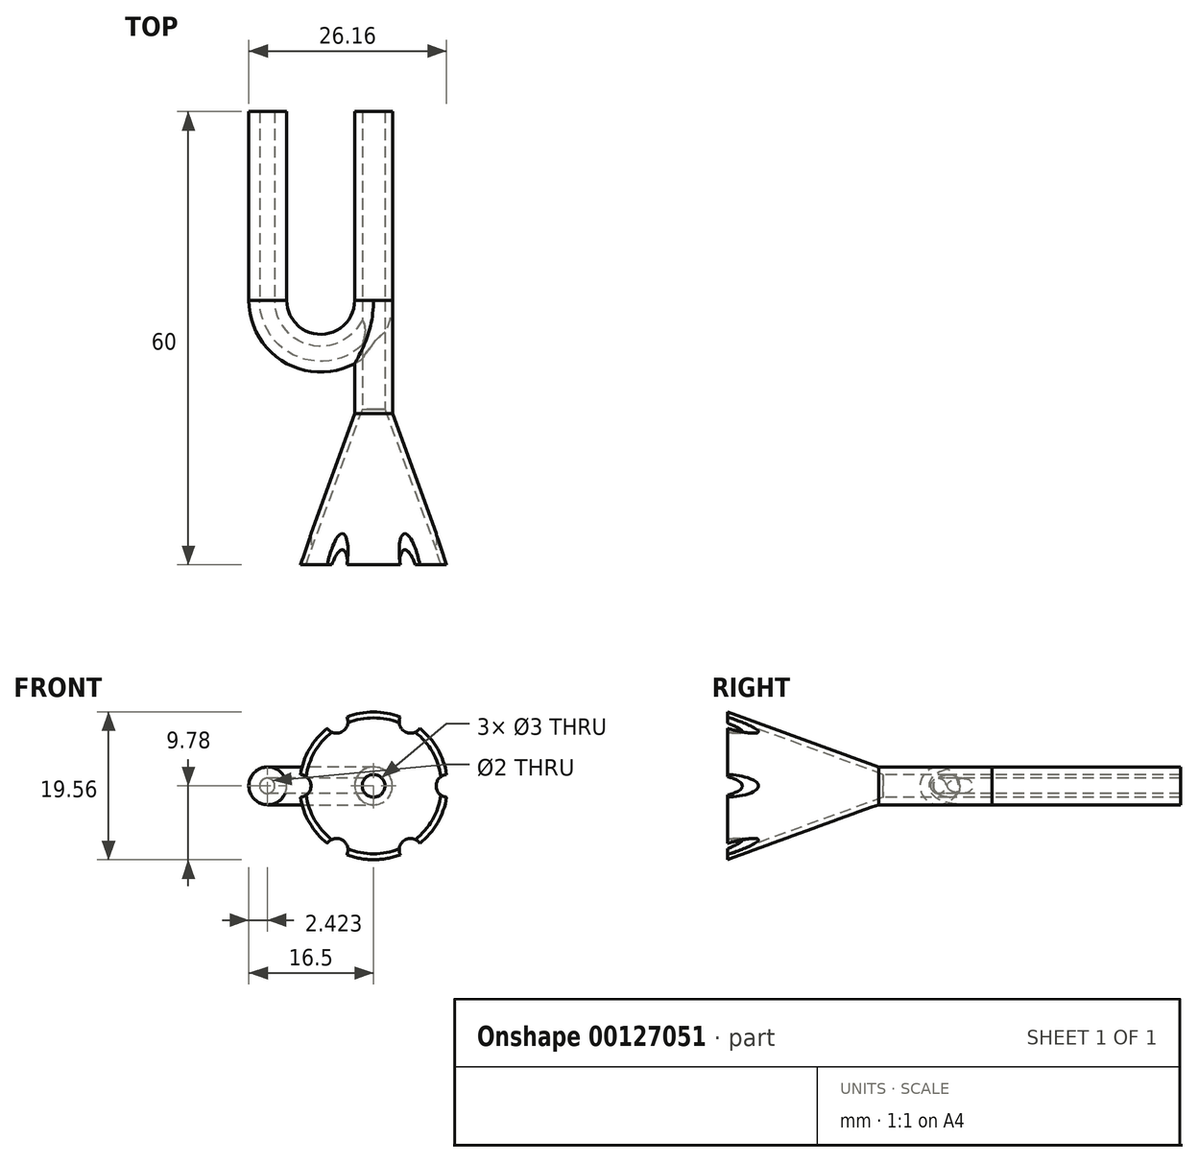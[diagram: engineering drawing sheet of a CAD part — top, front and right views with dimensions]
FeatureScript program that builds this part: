
annotation { "Feature Type Name" : "Feature", "Feature Type Description" : "" }
export const myFeature = defineFeature(function(context is Context, id is Id, definition is map)
    precondition{}
    {
        {
            var Q0;
            Q0=qCreatedBy(makeId("Top.planeOp"),FACE);
            var sketch = newSketch(context, id + "F0", { "sketchPlane" : qUnion([Q0])});
            skLineSegment(sketch, "E0.bottom", {"start": v(-11.15, 0) * mm, "end": v(11.15, 0) * mm});
            skLineSegment(sketch, "E0.top", {"start": v(-11.15, -35) * mm, "end": v(11.15, -35) * mm});
            skLineSegment(sketch, "E0.left", {"start": v(-11.15, 0) * mm, "end": v(-11.15, -35) * mm});
            skLineSegment(sketch, "E0.right", {"start": v(11.15, 0) * mm, "end": v(11.15, -35) * mm});
            skSolve(sketch);
        }
        {
            var Q0;
            Q0=qCreatedBy(makeId("Front.planeOp"),FACE);
            var sketch = newSketch(context, id + "F1", { "sketchPlane" : qUnion([Q0])});
            skCircle(sketch, "E1", {"center": v(7, 0) * mm, "radius": 2.5 * mm});
            skCircle(sketch, "E2", {"center": v(-7, 0) * mm, "radius": 2.5 * mm});
            skSolve(sketch);
        }
        {
            var Q0;
            Q0=makeQuery(id+"F1.imprint","IMPRINT",FACE,{"disambiguationData":[TD([[makeQuery(id+"F1.imprint","IMPRINT",EDGE,{"derivedFrom":sQuery(id+"F1.wireOp",EDGE,"E1")}),1.0]])]});
            extrude(context, id + "F2", {"entities" : qUnion([Q0]), "oppositeDirection" : true, "depth" : 25 * mm});
        }
        {
            var Q0;
            Q0=makeQuery(id+"F2.opExtrude","CAP_FACE",FACE,{"disambiguationData":[OSD([sQuery(id+"F1.wireOp",EDGE,"E1")])],"isStart":true});
            var sketch = newSketch(context, id + "F3", { "sketchPlane" : qUnion([Q0])});
            skCircle(sketch, "E3", {"center": v(7, 0) * mm, "radius": 1.5 * mm});
            skSolve(sketch);
        }
        {
            var Q0;
            Q0=makeQuery(id+"F1.imprint","IMPRINT",FACE,{"disambiguationData":[TD([[makeQuery(id+"F1.imprint","IMPRINT",EDGE,{"derivedFrom":sQuery(id+"F1.wireOp",EDGE,"E2")}),1.0]])]});
            var Q1;
            Q1=sQuery(id+"F1.wireOp",EDGE,"E2");
            extrude(context, id + "F4", {"entities" : qUnion([Q0]), "operationType" : NewBodyOperationType.ADD, "surfaceEntities" : qUnion([Q1]), "oppositeDirection" : true, "depth" : 25 * mm});
        }
        {
            var Q0;
            Q0=makeQuery(id+"F1.imprint","IMPRINT",FACE,{"disambiguationData":[TD([[makeQuery(id+"F1.imprint","IMPRINT",EDGE,{"derivedFrom":sQuery(id+"F1.wireOp",EDGE,"E2")}),1.0]])]});
            var sketch = newSketch(context, id + "F5", { "sketchPlane" : qUnion([Q0])});
            skCircle(sketch, "E4", {"center": v(-7.08, 0) * mm, "radius": 1 * mm});
            skSolve(sketch);
        }
        {
            var Q0;
            Q0 = qSketchRegion(id + "F5", true);
            extrude(context, id + "F6", {"entities" : qUnion([Q0]), "operationType" : NewBodyOperationType.REMOVE, "endBound" : BoundingType.THROUGH_ALL, "oppositeDirection" : true, "depth" : 25 * mm});
        }
        {
            var Q0;
            Q0=qCreatedBy(makeId("Top.planeOp"),FACE);
            var sketch = newSketch(context, id + "F7", { "sketchPlane" : qUnion([Q0])});
            skArc(sketch, "E5", {"start": v(-7, 0) * mm, "mid": v(0, -7) * mm, "end": v(7, 0) * mm});
            skSolve(sketch);
        }
        {
            var Q0;
            Q0=makeQuery(id+"F5.imprint","IMPRINT",FACE,{"disambiguationData":[TD([[makeQuery(id+"F5.imprint","IMPRINT",EDGE,{"derivedFrom":sQuery(id+"F5.wireOp",EDGE,"E4")}),-1.0]])]});
            var Q1;
            Q1=sQuery(id+"F7.wireOp",EDGE,"E5");
            sweep(context, id + "F8", {"profiles" : qUnion([Q0]), "path" : qUnion([Q1])});
        }
        {
            var Q0;
            Q0 = qSketchRegion(id + "F3", true);
            extrude(context, id + "F9", {"entities" : qUnion([Q0]), "operationType" : NewBodyOperationType.REMOVE, "oppositeDirection" : true, "depth" : 50 * mm, "symmetric" : true});
        }
        {
            var Q0;
            Q0=qCreatedBy(makeId("Front.planeOp"),FACE);
            cPlane(context, id + "F10", {"entities" : qUnion([Q0]), "cplaneType" : CPlaneType.OFFSET, "offset" : 15 * mm, "width" : 150 * mm, "height" : 150 * mm});
        }
        {
            var Q0;
            Q0=qCreatedBy(id+"F10.planeOp",FACE);
            var sketch = newSketch(context, id + "F11", { "sketchPlane" : qUnion([Q0])});
            skCircle(sketch, "E6", {"center": v(7, 0) * mm, "radius": 2.5 * mm});
            skSolve(sketch);
        }
        {
            var Q0;
            Q0=makeQuery(id+"F11.imprint","IMPRINT",FACE,{"disambiguationData":[TD([[makeQuery(id+"F11.imprint","IMPRINT",EDGE,{"derivedFrom":sQuery(id+"F11.wireOp",EDGE,"E6")}),1.0]])]});
            var Q1;
            Q1=makeQuery(id+"F8.opSweep","SWEPT_FACE",FACE,{"disambiguationData":[OSD([sQuery(id+"F1.wireOp",EDGE,"E2"),sQuery(id+"F7.wireOp",EDGE,"E5")])]});
            extrude(context, id + "F12", {"entities" : qUnion([Q0]), "endBound" : BoundingType.UP_TO_SURFACE, "oppositeDirection" : true, "endBoundEntityFace" : qUnion([Q1]), "depth" : 25 * mm});
        }
        {
            var Q0;
            Q0=makeQuery(id+"F12.opExtrude","CAP_FACE",FACE,{"disambiguationData":[OSD([sQuery(id+"F11.wireOp",EDGE,"E6")])],"isStart":true});
            var sketch = newSketch(context, id + "F13", { "sketchPlane" : qUnion([Q0])});
            skCircle(sketch, "E7", {"center": v(7, 0) * mm, "radius": 1.5 * mm});
            skSolve(sketch);
        }
        {
            var Q0;
            Q0 = qSketchRegion(id + "F13", true);
            var Q1;
            Q1=makeQuery(id+"F8.opSweep","SWEPT_FACE",FACE,{"disambiguationData":[OSD([sQuery(id+"F1.wireOp",EDGE,"E2"),sQuery(id+"F7.wireOp",EDGE,"E5")])]});
            extrude(context, id + "F14", {"entities" : qUnion([Q0]), "operationType" : NewBodyOperationType.REMOVE, "endBound" : BoundingType.UP_TO_SURFACE, "oppositeDirection" : true, "endBoundEntityFace" : qUnion([Q1]), "depth" : 25 * mm});
        }
        {
            var Q0;
            Q0=makeQuery(id+"F13.imprint","IMPRINT",FACE,{"disambiguationData":[TD([[makeQuery(id+"F13.imprint","IMPRINT",EDGE,{"derivedFrom":sQuery(id+"F13.wireOp",EDGE,"E7")}),-1.0]])]});
            extrude(context, id + "F15", {"entities" : qUnion([Q0]), "operationType" : NewBodyOperationType.ADD, "depth" : 20 * mm, "hasDraft" : true, "draftAngle" : 20 * degree});
        }
        {
            var Q0;
            Q0=makeQuery(id+"F15.opExtrude","CAP_FACE",FACE,{"disambiguationData":[OSD([sQuery(id+"F11.wireOp",EDGE,"E6"),sQuery(id+"F13.wireOp",EDGE,"E7")])],"isStart":false});
            var sketch = newSketch(context, id + "F16", { "sketchPlane" : qUnion([Q0])});
            skCircle(sketch, "E8", {"center": v(7, 0) * mm, "radius": 9 * mm});
            skCircle(sketch, "E9", {"center": v(-2.78, 0) * mm, "radius": 1.5 * mm});
            skCircle(sketch, "E10.1.0", {"center": v(2.11, 8.47) * mm, "radius": 1.5 * mm});
            skCircle(sketch, "E10.2.0", {"center": v(11.89, 8.47) * mm, "radius": 1.5 * mm});
            skCircle(sketch, "E10.3.0", {"center": v(16.78, 0) * mm, "radius": 1.5 * mm});
            skCircle(sketch, "E10.4.0", {"center": v(11.89, -8.47) * mm, "radius": 1.5 * mm});
            skCircle(sketch, "E10.5.0", {"center": v(2.11, -8.47) * mm, "radius": 1.5 * mm});
            skLineSegment(sketch, "E10.anchor1", {"start": v(7, 0) * mm, "end": v(-2.78, 0) * mm, "construction": true});
            skLineSegment(sketch, "E10.anchor2", {"start": v(7, 0) * mm, "end": v(2.11, -8.47) * mm, "construction": true});
            skSolve(sketch);
        }
        {
            var Q0;
            {var subQ0=sQuery(id+"F16.wireOp",EDGE,"E10.3.0");var subQ1=sQuery(id+"F16.wireOp",EDGE,"E8");var subQ2=makeQuery(id+"F16.imprint","INTERSECT",VERTEX,{"disambiguationData":[OD(0.0)],"derivedFrom":[subQ1,subQ0]});Q0=makeQuery(id+"F16.imprint","IMPRINT",FACE,{"disambiguationData":[TD([[makeQuery(id+"F16.imprint","IMPRINT",EDGE,{"disambiguationData":[TD([[subQ2,1.0]])],"derivedFrom":subQ1}),1.0]])]});}
            var Q1;
            {var subQ0=sQuery(id+"F16.wireOp",EDGE,"E10.4.0");var subQ1=sQuery(id+"F16.wireOp",EDGE,"E8");var subQ2=makeQuery(id+"F16.imprint","INTERSECT",VERTEX,{"disambiguationData":[OD(0.0)],"derivedFrom":[subQ1,subQ0]});Q1=makeQuery(id+"F16.imprint","IMPRINT",FACE,{"disambiguationData":[TD([[makeQuery(id+"F16.imprint","IMPRINT",EDGE,{"disambiguationData":[TD([[subQ2,-1.0]])],"derivedFrom":subQ1}),1.0]])]});}
            var Q2;
            {var subQ0=sQuery(id+"F16.wireOp",EDGE,"E10.5.0");var subQ1=sQuery(id+"F16.wireOp",EDGE,"E8");var subQ2=makeQuery(id+"F16.imprint","INTERSECT",VERTEX,{"disambiguationData":[OD(0.0)],"derivedFrom":[subQ1,subQ0]});Q2=makeQuery(id+"F16.imprint","IMPRINT",FACE,{"disambiguationData":[TD([[makeQuery(id+"F16.imprint","IMPRINT",EDGE,{"disambiguationData":[TD([[subQ2,-1.0]])],"derivedFrom":subQ1}),1.0]])]});}
            var Q3;
            {var subQ0=sQuery(id+"F16.wireOp",EDGE,"E9");var subQ1=sQuery(id+"F16.wireOp",EDGE,"E8");var subQ2=makeQuery(id+"F16.imprint","INTERSECT",VERTEX,{"disambiguationData":[OD(0.0)],"derivedFrom":[subQ1,subQ0]});Q3=makeQuery(id+"F16.imprint","IMPRINT",FACE,{"disambiguationData":[TD([[makeQuery(id+"F16.imprint","IMPRINT",EDGE,{"disambiguationData":[TD([[subQ2,-1.0]])],"derivedFrom":subQ1}),1.0]])]});}
            var Q4;
            {var subQ0=sQuery(id+"F16.wireOp",EDGE,"E10.1.0");var subQ1=sQuery(id+"F16.wireOp",EDGE,"E8");var subQ2=makeQuery(id+"F16.imprint","INTERSECT",VERTEX,{"disambiguationData":[OD(0.0)],"derivedFrom":[subQ1,subQ0]});Q4=makeQuery(id+"F16.imprint","IMPRINT",FACE,{"disambiguationData":[TD([[makeQuery(id+"F16.imprint","IMPRINT",EDGE,{"disambiguationData":[TD([[subQ2,-1.0]])],"derivedFrom":subQ1}),1.0]])]});}
            var Q5;
            {var subQ0=sQuery(id+"F16.wireOp",EDGE,"E10.2.0");var subQ1=sQuery(id+"F16.wireOp",EDGE,"E8");var subQ2=makeQuery(id+"F16.imprint","INTERSECT",VERTEX,{"disambiguationData":[OD(0.0)],"derivedFrom":[subQ1,subQ0]});Q5=makeQuery(id+"F16.imprint","IMPRINT",FACE,{"disambiguationData":[TD([[makeQuery(id+"F16.imprint","IMPRINT",EDGE,{"disambiguationData":[TD([[subQ2,-1.0]])],"derivedFrom":subQ1}),1.0]])]});}
            var Q6;
            {var subQ0=sQuery(id+"F16.wireOp",EDGE,"E10.2.0");var subQ1=sQuery(id+"F16.wireOp",EDGE,"E8");var subQ2=makeQuery(id+"F16.imprint","INTERSECT",VERTEX,{"disambiguationData":[OD(0.0)],"derivedFrom":[subQ1,subQ0]});Q6=makeQuery(id+"F16.imprint","IMPRINT",FACE,{"disambiguationData":[TD([[makeQuery(id+"F16.imprint","IMPRINT",EDGE,{"disambiguationData":[TD([[subQ2,1.0]])],"derivedFrom":subQ1}),1.0]])]});}
            extrude(context, id + "F17", {"entities" : qUnion([Q0, Q1, Q2, Q3, Q4, Q5, Q6]), "operationType" : NewBodyOperationType.REMOVE, "oppositeDirection" : true, "depth" : 25 * mm, "hasDraft" : true, "draftAngle" : 20 * degree, "draftPullDirection" : true});
        }
        {
            var Q0;
            {var subQ0=sQuery(id+"F16.wireOp",EDGE,"E9");var subQ1=sQuery(id+"F16.wireOp",EDGE,"E8");var subQ2=makeQuery(id+"F16.imprint","INTERSECT",VERTEX,{"disambiguationData":[OD(0.0)],"derivedFrom":[subQ1,subQ0]});Q0=makeQuery(id+"F16.imprint","IMPRINT",FACE,{"disambiguationData":[TD([[makeQuery(id+"F16.imprint","IMPRINT",EDGE,{"disambiguationData":[TD([[subQ2,-1.0]])],"derivedFrom":subQ1}),-1.0]])]});}
            var Q1;
            {var subQ0=sQuery(id+"F16.wireOp",EDGE,"E9");var subQ1=sQuery(id+"F16.wireOp",EDGE,"E8");var subQ2=makeQuery(id+"F16.imprint","INTERSECT",VERTEX,{"disambiguationData":[OD(0.0)],"derivedFrom":[subQ1,subQ0]});Q1=makeQuery(id+"F16.imprint","IMPRINT",FACE,{"disambiguationData":[TD([[makeQuery(id+"F16.imprint","IMPRINT",EDGE,{"disambiguationData":[TD([[subQ2,-1.0]])],"derivedFrom":subQ1}),1.0]])]});}
            var Q2;
            {var subQ0=sQuery(id+"F16.wireOp",EDGE,"E10.1.0");var subQ1=sQuery(id+"F16.wireOp",EDGE,"E8");var subQ2=makeQuery(id+"F16.imprint","INTERSECT",VERTEX,{"disambiguationData":[OD(0.0)],"derivedFrom":[subQ1,subQ0]});Q2=makeQuery(id+"F16.imprint","IMPRINT",FACE,{"disambiguationData":[TD([[makeQuery(id+"F16.imprint","IMPRINT",EDGE,{"disambiguationData":[TD([[subQ2,-1.0]])],"derivedFrom":subQ1}),1.0]])]});}
            var Q3;
            {var subQ0=sQuery(id+"F16.wireOp",EDGE,"E10.1.0");var subQ1=sQuery(id+"F16.wireOp",EDGE,"E8");var subQ2=makeQuery(id+"F16.imprint","INTERSECT",VERTEX,{"disambiguationData":[OD(0.0)],"derivedFrom":[subQ1,subQ0]});Q3=makeQuery(id+"F16.imprint","IMPRINT",FACE,{"disambiguationData":[TD([[makeQuery(id+"F16.imprint","IMPRINT",EDGE,{"disambiguationData":[TD([[subQ2,-1.0]])],"derivedFrom":subQ1}),-1.0]])]});}
            var Q4;
            {var subQ0=sQuery(id+"F16.wireOp",EDGE,"E10.2.0");var subQ1=sQuery(id+"F16.wireOp",EDGE,"E8");var subQ2=makeQuery(id+"F16.imprint","INTERSECT",VERTEX,{"disambiguationData":[OD(0.0)],"derivedFrom":[subQ1,subQ0]});Q4=makeQuery(id+"F16.imprint","IMPRINT",FACE,{"disambiguationData":[TD([[makeQuery(id+"F16.imprint","IMPRINT",EDGE,{"disambiguationData":[TD([[subQ2,-1.0]])],"derivedFrom":subQ1}),1.0]])]});}
            var Q5;
            {var subQ0=sQuery(id+"F16.wireOp",EDGE,"E10.2.0");var subQ1=sQuery(id+"F16.wireOp",EDGE,"E8");var subQ2=makeQuery(id+"F16.imprint","INTERSECT",VERTEX,{"disambiguationData":[OD(0.0)],"derivedFrom":[subQ1,subQ0]});Q5=makeQuery(id+"F16.imprint","IMPRINT",FACE,{"disambiguationData":[TD([[makeQuery(id+"F16.imprint","IMPRINT",EDGE,{"disambiguationData":[TD([[subQ2,-1.0]])],"derivedFrom":subQ1}),-1.0]])]});}
            var Q6;
            {var subQ0=sQuery(id+"F16.wireOp",EDGE,"E10.3.0");var subQ1=sQuery(id+"F16.wireOp",EDGE,"E8");var subQ2=makeQuery(id+"F16.imprint","INTERSECT",VERTEX,{"disambiguationData":[OD(0.0)],"derivedFrom":[subQ1,subQ0]});Q6=makeQuery(id+"F16.imprint","IMPRINT",FACE,{"disambiguationData":[TD([[makeQuery(id+"F16.imprint","IMPRINT",EDGE,{"disambiguationData":[TD([[subQ2,1.0]])],"derivedFrom":subQ1}),-1.0]])]});}
            var Q7;
            {var subQ0=sQuery(id+"F16.wireOp",EDGE,"E10.3.0");var subQ1=sQuery(id+"F16.wireOp",EDGE,"E8");var subQ2=makeQuery(id+"F16.imprint","INTERSECT",VERTEX,{"disambiguationData":[OD(0.0)],"derivedFrom":[subQ1,subQ0]});Q7=makeQuery(id+"F16.imprint","IMPRINT",FACE,{"disambiguationData":[TD([[makeQuery(id+"F16.imprint","IMPRINT",EDGE,{"disambiguationData":[TD([[subQ2,1.0]])],"derivedFrom":subQ1}),1.0]])]});}
            var Q8;
            {var subQ0=sQuery(id+"F16.wireOp",EDGE,"E10.4.0");var subQ1=sQuery(id+"F16.wireOp",EDGE,"E8");var subQ2=makeQuery(id+"F16.imprint","INTERSECT",VERTEX,{"disambiguationData":[OD(0.0)],"derivedFrom":[subQ1,subQ0]});Q8=makeQuery(id+"F16.imprint","IMPRINT",FACE,{"disambiguationData":[TD([[makeQuery(id+"F16.imprint","IMPRINT",EDGE,{"disambiguationData":[TD([[subQ2,-1.0]])],"derivedFrom":subQ1}),-1.0]])]});}
            var Q9;
            {var subQ0=sQuery(id+"F16.wireOp",EDGE,"E10.4.0");var subQ1=sQuery(id+"F16.wireOp",EDGE,"E8");var subQ2=makeQuery(id+"F16.imprint","INTERSECT",VERTEX,{"disambiguationData":[OD(0.0)],"derivedFrom":[subQ1,subQ0]});Q9=makeQuery(id+"F16.imprint","IMPRINT",FACE,{"disambiguationData":[TD([[makeQuery(id+"F16.imprint","IMPRINT",EDGE,{"disambiguationData":[TD([[subQ2,-1.0]])],"derivedFrom":subQ1}),1.0]])]});}
            var Q10;
            {var subQ0=sQuery(id+"F16.wireOp",EDGE,"E10.5.0");var subQ1=sQuery(id+"F16.wireOp",EDGE,"E8");var subQ2=makeQuery(id+"F16.imprint","INTERSECT",VERTEX,{"disambiguationData":[OD(0.0)],"derivedFrom":[subQ1,subQ0]});Q10=makeQuery(id+"F16.imprint","IMPRINT",FACE,{"disambiguationData":[TD([[makeQuery(id+"F16.imprint","IMPRINT",EDGE,{"disambiguationData":[TD([[subQ2,-1.0]])],"derivedFrom":subQ1}),-1.0]])]});}
            var Q11;
            {var subQ0=sQuery(id+"F16.wireOp",EDGE,"E10.5.0");var subQ1=sQuery(id+"F16.wireOp",EDGE,"E8");var subQ2=makeQuery(id+"F16.imprint","INTERSECT",VERTEX,{"disambiguationData":[OD(0.0)],"derivedFrom":[subQ1,subQ0]});Q11=makeQuery(id+"F16.imprint","IMPRINT",FACE,{"disambiguationData":[TD([[makeQuery(id+"F16.imprint","IMPRINT",EDGE,{"disambiguationData":[TD([[subQ2,-1.0]])],"derivedFrom":subQ1}),1.0]])]});}
            var Q12;
            Q12=sQuery(id+"F16.wireOp",EDGE,"E9");
            var Q13;
            Q13=sQuery(id+"F16.wireOp",EDGE,"E10.5.0");
            var Q14;
            Q14=sQuery(id+"F16.wireOp",EDGE,"E10.4.0");
            var Q15;
            Q15=sQuery(id+"F16.wireOp",EDGE,"E10.3.0");
            var Q16;
            Q16=sQuery(id+"F16.wireOp",EDGE,"E10.2.0");
            var Q17;
            Q17=sQuery(id+"F16.wireOp",EDGE,"E10.1.0");
            extrude(context, id + "F18", {"entities" : qUnion([Q0, Q1, Q2, Q3, Q4, Q5, Q6, Q7, Q8, Q9, Q10, Q11]), "operationType" : NewBodyOperationType.REMOVE, "surfaceEntities" : qUnion([Q12, Q13, Q14, Q15, Q16, Q17]), "oppositeDirection" : true, "depth" : 10 * mm});
        }
    });
